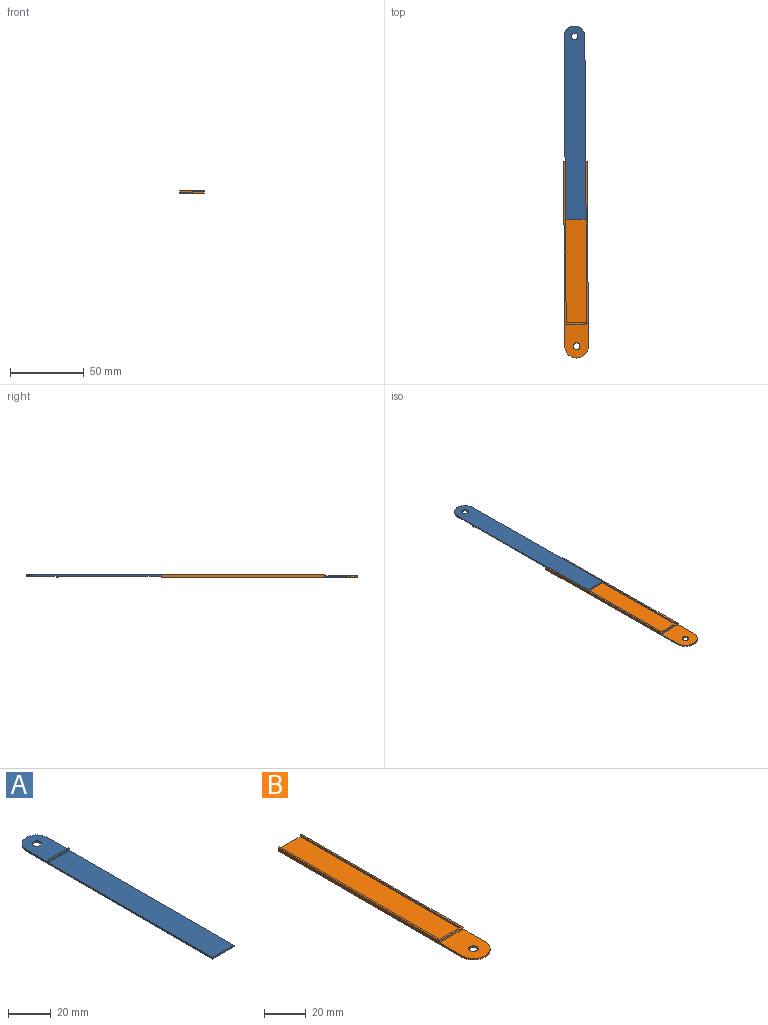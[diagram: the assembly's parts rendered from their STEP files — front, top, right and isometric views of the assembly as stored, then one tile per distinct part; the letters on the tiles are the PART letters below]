
ASSEMBLY  parts=2 mates=1
PART A: 11 faces, bbox 14x131x2 mm
  f0: plane 124x2mm, normal (-1,0,0), area 125mm2, adj f1,f3,f4,f5,f6,f7,f8,f9
  f1: plane 14x1mm, normal (0,-1,0), area 14mm2, adj f0,f2,f3,f4
  f2: plane 124x2mm, normal (1,0,0), area 125mm2, adj f1,f3,f4,f5,f6,f7,f8,f9
  f3: plane 109x14mm, normal (0,0,1), area 1526mm2, adj f0,f1,f2,f5
  f4: plane 131x14mm, normal (0,0,-1), area 1797.1mm2, adj f0,f1,f2,f8,f10
  f5: plane 14x1mm, normal (0,-1,0), area 14mm2, adj f0,f2,f3,f7
  f6: plane 14x1mm, normal (0,1,0), area 14mm2, adj f0,f2,f7,f9
  f7: plane 14x1mm, normal (0,0,1), area 14mm2, adj f0,f2,f5,f6
  f8: cylinder r=7mm len=14mm, axis (0,0,-1), area 22mm2, adj f0,f2,f4,f9
  f9: plane 21x14mm, normal (0,0,1), area 257.1mm2, adj f0,f2,f6,f8,f10
  f10: cylinder r=2.25mm len=4.5mm, axis (0,0,1), area 14.1mm2, adj f4,f9
PART B: 13 faces, bbox 16x133x2 mm
  f0: plane 16x2mm, normal (0,1,0), area 18mm2, adj f1,f2,f3,f5,f6,f8,f9
  f1: plane 109x14mm, normal (0,0,1), area 1526mm2, adj f0,f3,f4,f5
  f2: plane 133x16mm, normal (0,0,-1), area 2084.6mm2, adj f0,f6,f8,f10,f12
  f3: plane 109x1mm, normal (1,0,0), area 109mm2, adj f0,f1,f4,f9
  f4: plane 14x1mm, normal (0,1,0), area 14mm2, adj f1,f3,f5,f9
  f5: plane 109x1mm, normal (-1,0,0), area 109mm2, adj f0,f1,f4,f9
  f6: plane 125x2mm, normal (-1,0,0), area 235mm2, adj f0,f2,f7,f9,f10,f11
  f7: plane 16x1mm, normal (0,-1,0), area 16mm2, adj f6,f8,f9,f11
  f8: plane 125x2mm, normal (1,0,0), area 235mm2, adj f0,f2,f7,f9,f10,f11
  f9: plane 110x16mm, normal (0,0,1), area 234mm2, adj f0,f3,f4,f5,f6,f7,f8
  f10: cylinder r=8mm len=16mm, axis (0,0,-1), area 25.1mm2, adj f2,f6,f8,f11
  f11: plane 23x16mm, normal (0,0,1), area 324.6mm2, adj f6,f7,f8,f10,f12
  f12: cylinder r=2.25mm len=4.5mm, axis (0,0,-1), area 14.1mm2, adj f2,f11
PLACE A rot(axis=(0,1,0),180deg) t=(10.93,89.42,12.77)mm
PLACE B rot(axis=(0,0,1),0.4deg) t=(18.53,19.47,10.77)mm
MATE slider A.f1 <-> B.f4  axis (0.01,-1,0) through (28.22,44.29,12.27)mm
